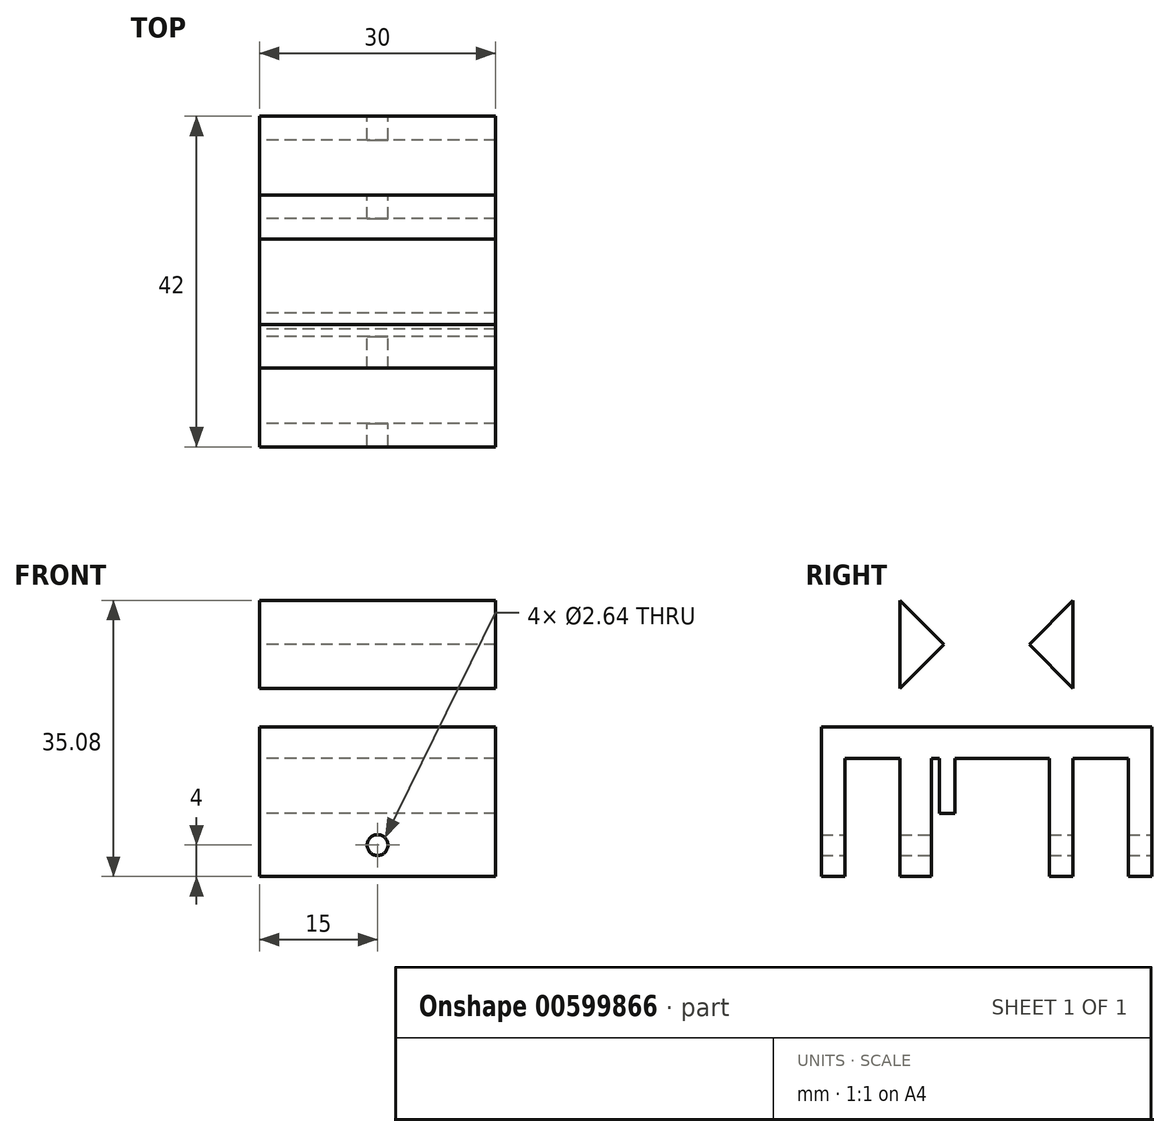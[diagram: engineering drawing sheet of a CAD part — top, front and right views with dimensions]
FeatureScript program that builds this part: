
annotation { "Feature Type Name" : "Feature", "Feature Type Description" : "" }
export const myFeature = defineFeature(function(context is Context, id is Id, definition is map)
    precondition{}
    {
        {
            var Q0;
            Q0=qCreatedBy(makeId("Right.planeOp"),FACE);
            var sketch = newSketch(context, id + "F0", { "sketchPlane" : qUnion([Q0])});
            skLineSegment(sketch, "E0.bottom", {"start": v(-21, 0) * mm, "end": v(21, 0) * mm});
            skLineSegment(sketch, "E0.top", {"start": v(-21, 4) * mm, "end": v(21, 4) * mm});
            skLineSegment(sketch, "E0.left", {"start": v(-21, 0) * mm, "end": v(-21, 4) * mm});
            skLineSegment(sketch, "E0.right", {"start": v(21, 0) * mm, "end": v(21, 4) * mm});
            skLineSegment(sketch, "E1.bottom", {"start": v(21, 4) * mm, "end": v(11, 4) * mm});
            skLineSegment(sketch, "E1.top", {"start": v(21, 25) * mm, "end": v(11, 25) * mm});
            skLineSegment(sketch, "E1.left", {"start": v(21, 4) * mm, "end": v(21, 25) * mm});
            skLineSegment(sketch, "E1.right", {"start": v(11, 4) * mm, "end": v(11, 25) * mm});
            skLineSegment(sketch, "E2", {"start": v(0, 0) * mm, "end": v(0, 12.87) * mm});
            skLineSegment(sketch, "E3.MirrorCS", {"start": v(-11, 4) * mm, "end": v(-11, 25) * mm});
            skLineSegment(sketch, "E4.MirrorCS", {"start": v(-21, 25) * mm, "end": v(-11, 25) * mm});
            skLineSegment(sketch, "E5.MirrorCS", {"start": v(-21, 4) * mm, "end": v(-21, 25) * mm});
            skLineSegment(sketch, "E6.MirrorCS", {"start": v(-21, 4) * mm, "end": v(-11, 4) * mm});
            skLineSegment(sketch, "E7", {"start": v(11, 20.08) * mm, "end": v(5.42, 14.5) * mm});
            skPoint(sketch, "E7.endSnap0", {"position": v(11, 14.5) * mm});
            skLineSegment(sketch, "E8", {"start": v(5.42, 14.5) * mm, "end": v(11, 8.92) * mm});
            skLineSegment(sketch, "E9.MirrorCS", {"start": v(-5.42, 14.5) * mm, "end": v(-11, 8.92) * mm});
            skLineSegment(sketch, "E10.MirrorCS", {"start": v(-11, 20.08) * mm, "end": v(-5.42, 14.5) * mm});
            skLineSegment(sketch, "E11", {"start": v(-13, 25) * mm, "end": v(-21, 4) * mm});
            skLineSegment(sketch, "E12", {"start": v(13, 25) * mm, "end": v(21, 4) * mm});
            skSolve(sketch);
        }
        {
            var Q0;
            {var subQ0=sQuery(id+"F0.wireOp",EDGE,"E7");Q0=makeQuery(id+"F0.imprint","IMPRINT",FACE,{"disambiguationData":[TD([[makeQuery(id+"F0.imprint","IMPRINT",EDGE,{"derivedFrom":subQ0}),1.0]])]});}
            var Q1;
            {var subQ0=sQuery(id+"F0.wireOp",EDGE,"E9.MirrorCS");Q1=makeQuery(id+"F0.imprint","IMPRINT",FACE,{"disambiguationData":[TD([[makeQuery(id+"F0.imprint","IMPRINT",EDGE,{"derivedFrom":subQ0}),-1.0]])]});}
            var Q2;
            {var subQ5=sQuery(id+"F0.wireOp",EDGE,"E0.left");Q2=makeQuery(id+"F0.imprint","IMPRINT",FACE,{"disambiguationData":[TD([[makeQuery(id+"F0.imprint","IMPRINT",EDGE,{"derivedFrom":subQ5}),-1.0]])]});}
            var Q3;
            {var subQ1=sQuery(id+"F0.wireOp",EDGE,"E0.right");Q3=makeQuery(id+"F0.imprint","IMPRINT",FACE,{"disambiguationData":[TD([[makeQuery(id+"F0.imprint","IMPRINT",EDGE,{"derivedFrom":subQ1}),1.0]])]});}
            var Q4;
            {var subQ4=sQuery(id+"F0.wireOp",EDGE,"E1.bottom");Q4=makeQuery(id+"F0.imprint","IMPRINT",FACE,{"disambiguationData":[TD([[makeQuery(id+"F0.imprint","IMPRINT",EDGE,{"derivedFrom":subQ4}),-1.0]])]});}
            var Q5;
            {var subQ0=sQuery(id+"F0.wireOp",EDGE,"E6.MirrorCS");Q5=makeQuery(id+"F0.imprint","IMPRINT",FACE,{"disambiguationData":[TD([[makeQuery(id+"F0.imprint","IMPRINT",EDGE,{"derivedFrom":subQ0}),1.0]])]});}
            extrude(context, id + "F1", {"entities" : qUnion([Q0, Q1, Q2, Q3, Q4, Q5]), "depth" : 30 * mm});
        }
        {
            var Q0;
            Q0=qCreatedBy(makeId("Right.planeOp"),FACE);
            var sketch = newSketch(context, id + "F2", { "sketchPlane" : qUnion([Q0])});
            skLineSegment(sketch, "E13.bottom", {"start": v(-11, 0) * mm, "end": v(-7, 0) * mm});
            skLineSegment(sketch, "E13.top", {"start": v(-11, -15) * mm, "end": v(-7, -15) * mm});
            skLineSegment(sketch, "E13.left", {"start": v(-7, 0) * mm, "end": v(-7, -15) * mm});
            skLineSegment(sketch, "E13.right", {"start": v(-11, 0) * mm, "end": v(-11, -15) * mm});
            skLineSegment(sketch, "E14.bottom", {"start": v(8, 0) * mm, "end": v(11, 0) * mm});
            skLineSegment(sketch, "E14.top", {"start": v(8, -15) * mm, "end": v(11, -15) * mm});
            skLineSegment(sketch, "E14.left", {"start": v(8, 0) * mm, "end": v(8, -15) * mm});
            skLineSegment(sketch, "E14.right", {"start": v(11, 0) * mm, "end": v(11, -15) * mm});
            skLineSegment(sketch, "E15.bottom", {"start": v(18, 0) * mm, "end": v(21, 0) * mm});
            skLineSegment(sketch, "E15.top", {"start": v(18, -15) * mm, "end": v(21, -15) * mm});
            skLineSegment(sketch, "E15.left", {"start": v(21, 0) * mm, "end": v(21, -15) * mm});
            skLineSegment(sketch, "E15.right", {"start": v(18, 0) * mm, "end": v(18, -15) * mm});
            skLineSegment(sketch, "E16.bottom", {"start": v(-21, 0) * mm, "end": v(-18, 0) * mm});
            skLineSegment(sketch, "E16.top", {"start": v(-21, -15) * mm, "end": v(-18, -15) * mm});
            skLineSegment(sketch, "E16.left", {"start": v(-21, 0) * mm, "end": v(-21, -15) * mm});
            skLineSegment(sketch, "E16.right", {"start": v(-18, 0) * mm, "end": v(-18, -15) * mm});
            skLineSegment(sketch, "E17.bottom", {"start": v(-6, 0) * mm, "end": v(0, 0) * mm});
            skLineSegment(sketch, "E17.top", {"start": v(-6, -7) * mm, "end": v(-4, -7) * mm});
            skLineSegment(sketch, "E17.left", {"start": v(-6, 0) * mm, "end": v(-6, -7) * mm});
            skLineSegment(sketch, "E17.right", {"start": v(-4, 0) * mm, "end": v(-4, -7) * mm});
            skLineSegment(sketch, "E18", {"start": v(6, 0) * mm, "end": v(6, -15.6) * mm});
            skSolve(sketch);
        }
        {
            var Q0;
            Q0=makeQuery(id+"F2.imprint","IMPRINT",FACE,{"disambiguationData":[TD([[makeQuery(id+"F2.imprint","IMPRINT",EDGE,{"derivedFrom":sQuery(id+"F2.wireOp",EDGE,"E16.bottom")}),-1.0]])]});
            var Q1;
            Q1=makeQuery(id+"F2.imprint","IMPRINT",FACE,{"disambiguationData":[TD([[makeQuery(id+"F2.imprint","IMPRINT",EDGE,{"derivedFrom":sQuery(id+"F2.wireOp",EDGE,"E14.bottom")}),-1.0]])]});
            var Q2;
            Q2=makeQuery(id+"F2.imprint","IMPRINT",FACE,{"disambiguationData":[TD([[makeQuery(id+"F2.imprint","IMPRINT",EDGE,{"derivedFrom":sQuery(id+"F2.wireOp",EDGE,"E15.bottom")}),-1.0]])]});
            var Q3;
            Q3=makeQuery(id+"F1.opExtrude","CAP_FACE",FACE,{"disambiguationData":[OSD([sQuery(id+"F0.wireOp",EDGE,"E0.bottom"),sQuery(id+"F0.wireOp",EDGE,"E0.top"),sQuery(id+"F0.wireOp",EDGE,"E0.left"),sQuery(id+"F0.wireOp",EDGE,"E0.right"),sQuery(id+"F0.wireOp",EDGE,"E1.top"),sQuery(id+"F0.wireOp",EDGE,"E1.left"),sQuery(id+"F0.wireOp",EDGE,"E1.right"),sQuery(id+"F0.wireOp",EDGE,"E4.MirrorCS"),sQuery(id+"F0.wireOp",EDGE,"E5.MirrorCS"),sQuery(id+"F0.wireOp",EDGE,"E3.MirrorCS"),sQuery(id+"F0.wireOp",EDGE,"E7"),sQuery(id+"F0.wireOp",EDGE,"E8"),sQuery(id+"F0.wireOp",EDGE,"E9.MirrorCS"),sQuery(id+"F0.wireOp",EDGE,"E10.MirrorCS")])],"isStart":false});
            extrude(context, id + "F3", {"entities" : qUnion([Q0, Q1, Q2]), "operationType" : NewBodyOperationType.ADD, "endBound" : BoundingType.UP_TO_SURFACE, "endBoundEntityFace" : qUnion([Q3]), "depth" : 10 * mm});
        }
        {
            var Q0;
            Q0=makeQuery(id+"F2.imprint","IMPRINT",FACE,{"disambiguationData":[TD([[makeQuery(id+"F2.imprint","IMPRINT",EDGE,{"derivedFrom":sQuery(id+"F2.wireOp",EDGE,"E13.bottom")}),-1.0]])]});
            var Q1;
            Q1=makeQuery(id+"F1.opExtrude","CAP_FACE",FACE,{"disambiguationData":[OSD([sQuery(id+"F0.wireOp",EDGE,"E0.bottom"),sQuery(id+"F0.wireOp",EDGE,"E0.top"),sQuery(id+"F0.wireOp",EDGE,"E0.left"),sQuery(id+"F0.wireOp",EDGE,"E0.right"),sQuery(id+"F0.wireOp",EDGE,"E1.top"),sQuery(id+"F0.wireOp",EDGE,"E1.left"),sQuery(id+"F0.wireOp",EDGE,"E1.right"),sQuery(id+"F0.wireOp",EDGE,"E4.MirrorCS"),sQuery(id+"F0.wireOp",EDGE,"E5.MirrorCS"),sQuery(id+"F0.wireOp",EDGE,"E3.MirrorCS"),sQuery(id+"F0.wireOp",EDGE,"E7"),sQuery(id+"F0.wireOp",EDGE,"E8"),sQuery(id+"F0.wireOp",EDGE,"E9.MirrorCS"),sQuery(id+"F0.wireOp",EDGE,"E10.MirrorCS")])],"isStart":false});
            extrude(context, id + "F4", {"entities" : qUnion([Q0]), "operationType" : NewBodyOperationType.ADD, "endBound" : BoundingType.UP_TO_SURFACE, "endBoundEntityFace" : qUnion([Q1]), "depth" : 25 * mm});
        }
        {
            var Q0;
            Q0=makeQuery(id+"F2.imprint","IMPRINT",FACE,{"disambiguationData":[TD([[makeQuery(id+"F2.imprint","IMPRINT",EDGE,{"derivedFrom":sQuery(id+"F2.wireOp",EDGE,"E17.top")}),1.0]])]});
            var Q1;
            Q1=makeQuery(id+"F1.opExtrude","CAP_FACE",FACE,{"disambiguationData":[OSD([sQuery(id+"F0.wireOp",EDGE,"E0.bottom"),sQuery(id+"F0.wireOp",EDGE,"E0.top"),sQuery(id+"F0.wireOp",EDGE,"E0.left"),sQuery(id+"F0.wireOp",EDGE,"E0.right"),sQuery(id+"F0.wireOp",EDGE,"E1.top"),sQuery(id+"F0.wireOp",EDGE,"E1.left"),sQuery(id+"F0.wireOp",EDGE,"E1.right"),sQuery(id+"F0.wireOp",EDGE,"E4.MirrorCS"),sQuery(id+"F0.wireOp",EDGE,"E5.MirrorCS"),sQuery(id+"F0.wireOp",EDGE,"E3.MirrorCS"),sQuery(id+"F0.wireOp",EDGE,"E7"),sQuery(id+"F0.wireOp",EDGE,"E8"),sQuery(id+"F0.wireOp",EDGE,"E9.MirrorCS"),sQuery(id+"F0.wireOp",EDGE,"E10.MirrorCS")])],"isStart":false});
            extrude(context, id + "F5", {"entities" : qUnion([Q0]), "operationType" : NewBodyOperationType.ADD, "endBound" : BoundingType.UP_TO_SURFACE, "endBoundEntityFace" : qUnion([Q1]), "depth" : 25 * mm});
        }
        {
            var Q0;
            Q0=makeQuery(id+"F3.boolean.opBoolean","MERGE",FACE,{"derivedFrom":[makeQuery(id+"F1.opExtrude","SWEPT_FACE",FACE,{"disambiguationData":[OSD([sQuery(id+"F0.wireOp",EDGE,"E0.right"),sQuery(id+"F0.wireOp",EDGE,"E1.left")])]}),makeQuery(id+"F3.opExtrude","SWEPT_FACE",FACE,{"disambiguationData":[OSD([sQuery(id+"F2.wireOp",EDGE,"E15.left")])]})]});
            var sketch = newSketch(context, id + "F6", { "sketchPlane" : qUnion([Q0])});
            skLineSegment(sketch, "E19", {"start": v(0, -11) * mm, "end": v(-30, -11) * mm});
            skLineSegment(sketch, "E20", {"start": v(-15, -15) * mm, "end": v(-15, -6.7) * mm});
            skPoint(sketch, "E21", {"position": v(-15, -11) * mm});
            skSolve(sketch);
        }
        {
            var Q0;
            Q0=sQuery(id+"F6.wireOp",VERTEX,"E21");
            var Q1;
            Q1=makeQuery(id+"F1.opExtrude","SWEPT_BODY",BODY,{"disambiguationData":[OSD([sQuery(id+"F0.wireOp",EDGE,"E0.bottom"),sQuery(id+"F0.wireOp",EDGE,"E0.top"),sQuery(id+"F0.wireOp",EDGE,"E0.left"),sQuery(id+"F0.wireOp",EDGE,"E0.right"),sQuery(id+"F0.wireOp",EDGE,"E1.top"),sQuery(id+"F0.wireOp",EDGE,"E1.left"),sQuery(id+"F0.wireOp",EDGE,"E1.right"),sQuery(id+"F0.wireOp",EDGE,"E4.MirrorCS"),sQuery(id+"F0.wireOp",EDGE,"E5.MirrorCS"),sQuery(id+"F0.wireOp",EDGE,"E3.MirrorCS"),sQuery(id+"F0.wireOp",EDGE,"E7"),sQuery(id+"F0.wireOp",EDGE,"E8"),sQuery(id+"F0.wireOp",EDGE,"E9.MirrorCS"),sQuery(id+"F0.wireOp",EDGE,"E10.MirrorCS")])]});
            hole(context, id + "F7", {"style" : HoleStyle.SIMPLE, "endStyle" : HoleEndStyle.THROUGH, "standardTappedOrClearance" : lookupTablePath({ "standard" : "ANSI", "fit" : "Close", "size" : "#3", "type" : "Clearance" }), "standardBlindInLast" : lookupTablePath({ "fit" : "Close", "standard" : "ANSI", "size" : "#3", "type" : "Clearance" }), "holeDiameter" : 2.64 * mm, "locations" : qUnion([Q0]), "scope" : qUnion([Q1]), "isTappedThrough" : true});
        }
    });
